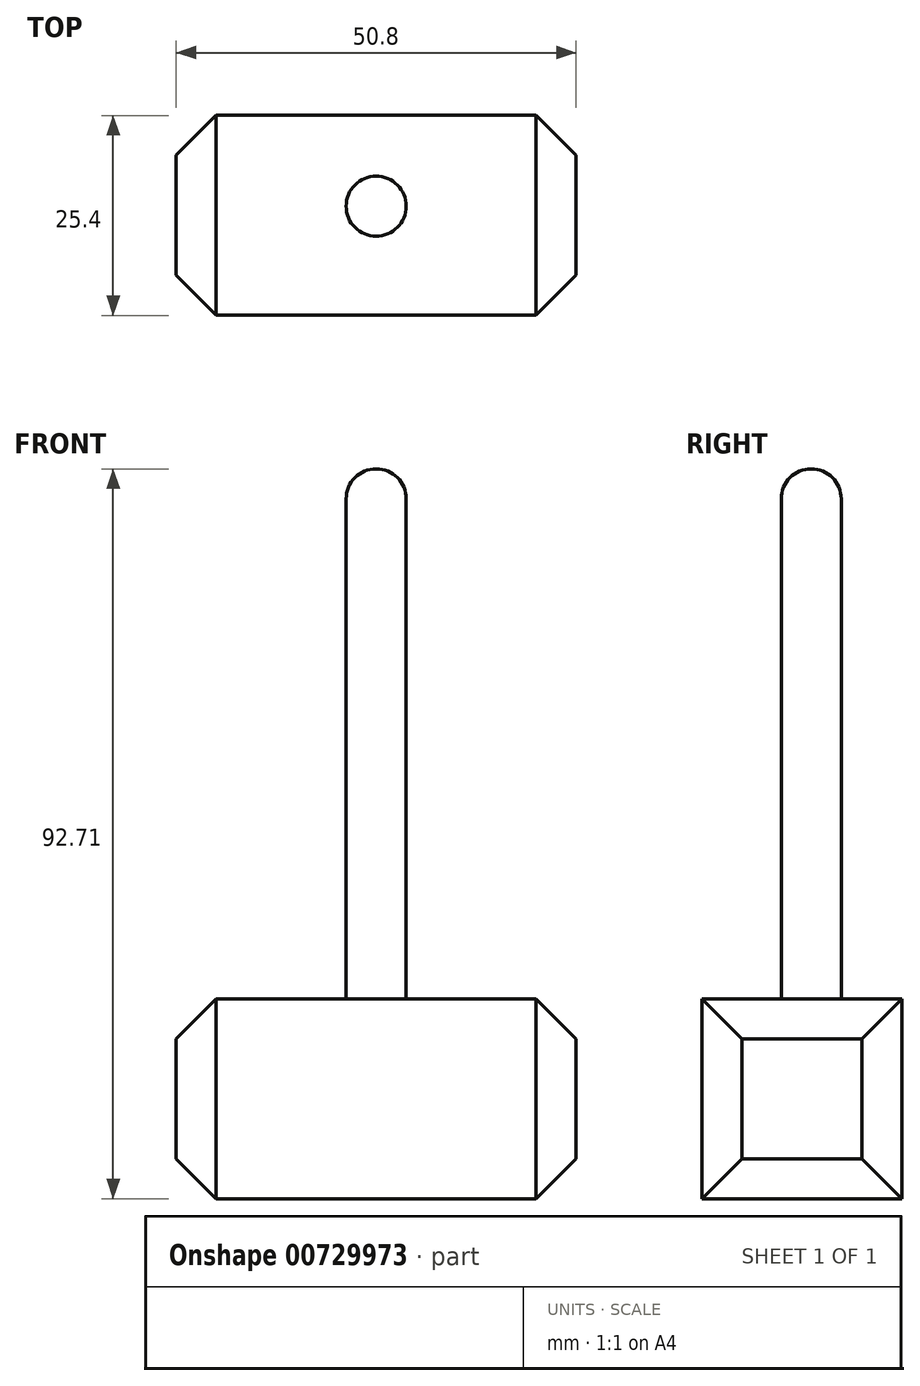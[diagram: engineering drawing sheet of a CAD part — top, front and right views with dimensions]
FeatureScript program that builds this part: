
annotation { "Feature Type Name" : "Feature", "Feature Type Description" : "" }
export const myFeature = defineFeature(function(context is Context, id is Id, definition is map)
    precondition{}
    {
        {
            var Q0;
            Q0=qCreatedBy(makeId("Top.planeOp"),FACE);
            var sketch = newSketch(context, id + "F0", { "sketchPlane" : qUnion([Q0])});
            skLineSegment(sketch, "E0.bottom", {"start": v(25.4, -13.87) * mm, "end": v(-25.4, -13.87) * mm});
            skLineSegment(sketch, "E0.top", {"start": v(25.4, 11.53) * mm, "end": v(-25.4, 11.53) * mm});
            skLineSegment(sketch, "E0.left", {"start": v(25.4, -13.87) * mm, "end": v(25.4, 11.53) * mm});
            skLineSegment(sketch, "E0.right", {"start": v(-25.4, -13.87) * mm, "end": v(-25.4, 11.53) * mm});
            skPoint(sketch, "E0.middle", {"position": v(0, -1.17) * mm});
            skSolve(sketch);
        }
        {
            var Q0;
            Q0=makeQuery(id+"F0.imprint","IMPRINT",FACE,{"disambiguationData":[TD([[makeQuery(id+"F0.imprint","IMPRINT",EDGE,{"derivedFrom":sQuery(id+"F0.wireOp",EDGE,"E0.bottom")}),-1.0]])]});
            extrude(context, id + "F1", {"entities" : qUnion([Q0]), "depth" : 25.4 * mm, "offsetDistance" : 25.4 * mm});
        }
        {
            var Q0;
            Q0=makeQuery(id+"F1.opExtrude","CAP_FACE",FACE,{"disambiguationData":[OSD([sQuery(id+"F0.wireOp",EDGE,"E0.bottom"),sQuery(id+"F0.wireOp",EDGE,"E0.top"),sQuery(id+"F0.wireOp",EDGE,"E0.left"),sQuery(id+"F0.wireOp",EDGE,"E0.right")])],"isStart":false});
            var sketch = newSketch(context, id + "F2", { "sketchPlane" : qUnion([Q0])});
            skCircle(sketch, "E1", {"center": v(0, 0) * mm, "radius": 3.81 * mm});
            skSolve(sketch);
        }
        {
            var Q0;
            Q0=makeQuery(id+"F2.imprint","IMPRINT",FACE,{"disambiguationData":[TD([[makeQuery(id+"F2.imprint","IMPRINT",EDGE,{"derivedFrom":sQuery(id+"F2.wireOp",EDGE,"E1")}),1.0]])]});
            extrude(context, id + "F3", {"entities" : qUnion([Q0]), "operationType" : NewBodyOperationType.ADD, "depth" : 63.5 * mm, "offsetDistance" : 25.4 * mm});
        }
        {
            var Q0;
            Q0=makeQuery(id+"F3.opExtrude","CAP_FACE",FACE,{"disambiguationData":[OSD([sQuery(id+"F2.wireOp",EDGE,"E1")])],"isStart":false});
            var sketch = newSketch(context, id + "F4", { "sketchPlane" : qUnion([Q0])});
            skArc(sketch, "E2", {"start": v(0, -3.81) * mm, "mid": v(3.84, 0) * mm, "end": v(0, 3.81) * mm});
            skLineSegment(sketch, "E3", {"start": v(0, 3.81) * mm, "end": v(0, -3.81) * mm});
            skSolve(sketch);
        }
        {
            var Q0;
            {var subQ0=sQuery(id+"F4.wireOp",EDGE,"E3");Q0=makeQuery(id+"F4.imprint","IMPRINT",FACE,{"disambiguationData":[TD([[makeQuery(id+"F4.imprint","IMPRINT",EDGE,{"derivedFrom":subQ0}),1.0]])]});}
            var Q1;
            Q1=sQuery(id+"F4.wireOp",EDGE,"E3");
            revolve(context, id + "F5", {"operationType" : NewBodyOperationType.ADD, "surfaceOperationType" : NewSurfaceOperationType.NEW, "entities" : qUnion([Q0]), "axis" : qUnion([Q1]), "revolveType" : RevolveType.FULL});
        }
        {
            var Q0;
            Q0=makeQuery(id+"F1.opExtrude","SWEPT_EDGE",EDGE,{"disambiguationData":[OSD([sQuery(id+"F0.wireOp",EDGE,"E0.top"),sQuery(id+"F0.wireOp",EDGE,"E0.right")])]});
            var Q1;
            Q1=makeQuery(id+"F1.opExtrude","CAP_EDGE",EDGE,{"disambiguationData":[OSD([sQuery(id+"F0.wireOp",EDGE,"E0.right")])],"isStart":false});
            var Q2;
            Q2=makeQuery(id+"F1.opExtrude","CAP_EDGE",EDGE,{"disambiguationData":[OSD([sQuery(id+"F0.wireOp",EDGE,"E0.left")])],"isStart":false});
            var Q3;
            Q3=makeQuery(id+"F1.opExtrude","SWEPT_EDGE",EDGE,{"disambiguationData":[OSD([sQuery(id+"F0.wireOp",EDGE,"E0.top"),sQuery(id+"F0.wireOp",EDGE,"E0.left")])]});
            var Q4;
            Q4=makeQuery(id+"F1.opExtrude","CAP_EDGE",EDGE,{"disambiguationData":[OSD([sQuery(id+"F0.wireOp",EDGE,"E0.left")])],"isStart":true});
            var Q5;
            Q5=makeQuery(id+"F1.opExtrude","SWEPT_EDGE",EDGE,{"disambiguationData":[OSD([sQuery(id+"F0.wireOp",EDGE,"E0.bottom"),sQuery(id+"F0.wireOp",EDGE,"E0.left")])]});
            var Q6;
            Q6=makeQuery(id+"F1.opExtrude","SWEPT_EDGE",EDGE,{"disambiguationData":[OSD([sQuery(id+"F0.wireOp",EDGE,"E0.bottom"),sQuery(id+"F0.wireOp",EDGE,"E0.right")])]});
            var Q7;
            Q7=makeQuery(id+"F1.opExtrude","CAP_EDGE",EDGE,{"disambiguationData":[OSD([sQuery(id+"F0.wireOp",EDGE,"E0.right")])],"isStart":true});
            chamfer(context, id + "F6", {"entities" : qUnion([Q0, Q1, Q2, Q3, Q4, Q5, Q6, Q7]), "width" : 5.08 * mm, "tangentPropagation" : true});
        }
    });
